# Revit family: Mailboxes_4C-Salsbury_Industries-Rear_Load-9_Door_High_Units
name_source: partatom
category: Specialty Equipment
revit_build: Autodesk Revit 2016 (Build: 20150714_1515(x64)
units: mm (PartAtom-declared; Revit-internal decimal feet)

## family parameters
Always vertical = Yes
Cut with Voids When Loaded = No
Host = Wall
OmniClass Number = 23.40.90.14.11
OmniClass Title = Mail Boxes
Part Type = Normal
Room Calculation Point = No
Round Connector Dimension = Use Diameter
Shared = No

## types (13) — shared parameters
Assembly Code = C1030910
Assembly Description = Mailboxes
Back Enclosure Material = Aluminum - Salsbury Finish - Anodized
Bottom Back Plate = No
Depth = 17.025"
Height = 34.000"
Latch Distance = 9.515"
Latch Locks-Right Side = Yes
Lock Material = Stainless Steel - Salsbury Finish -  Polished
Manufacturer = Salsbury Industries
MasterFormat Number = 10 55 00
MasterFormat Title = Postal Specialties
OmniClass 23 Number = 23.40.90.14.11
OmniClass 23 Title = Mail Boxes
Top Back Plate = No
URL = www.mailboxes.com
Version = 3.0 (06/30/17)

## per-type parameters (varying)
- 3709S-1B RL: Description=9 Door High Unit; Door Slot L1=3700 Series 4C Door Configurations : Empty; Door Slot L2=3700 Series 4C Door Configurations : Empty; Door Slot L3=3700 Series 4C Door Configurations : Empty; Door Slot L4=3700 Series 4C Door Configurations : Empty; Door Slot L5=3700 Series 4C Door Configurations : Empty; Door Slot L6=3700 Series 4C Door Configurations : Empty; Door Slot L7=3700 Series 4C Door Configurations : Empty; Door Slot L8=3700 Series 4C Door Configurations : Empty; Door Slot L9=3700 Series 4C Door Configurations : Empty; Door Slot R1=3700 Series 4C Door Configurations : Empty; Door Slot R2=3700 Series 4C Door Configurations : Empty; Door Slot R3=3700 Series 4C Door Configurations : Empty; Door Slot R4=3700 Series 4C Door Configurations : Empty; Door Slot R5=3700 Series 4C Door Configurations : Empty; Door Slot R6=3700 Series 4C Door Configurations : Empty; Door Slot R7=3700 Series 4C Door Configurations : Empty; Door Slot R8=3700 Series 4C Door Configurations : Empty; Door Slot R9=4C-9 Door High Receptacle; Latch Alignment=13.876"; Latch Locks-Left Side=No; Left Inside Wall=No; Right Inside Wall=No; Type Comments=4C Horizontal Receptacle Bin - Rear Loading; Vertical Center Divider=No; Width=16.344"
- 3709S-1C RL: Description=9 Door High Unit; Door Slot L1=3700 Series 4C Door Configurations : Empty; Door Slot L2=3700 Series 4C Door Configurations : Empty; Door Slot L3=3700 Series 4C Door Configurations : Empty; Door Slot L4=3700 Series 4C Door Configurations : Empty; Door Slot L5=3700 Series 4C Door Configurations : Empty; Door Slot L6=3700 Series 4C Door Configurations : Empty; Door Slot L7=3700 Series 4C Door Configurations : Empty; Door Slot L8=3700 Series 4C Door Configurations : Empty; Door Slot L9=3700 Series 4C Door Configurations : Empty; Door Slot R1=3700 Series 4C Door Configurations : Empty; Door Slot R2=3700 Series 4C Door Configurations : Empty; Door Slot R3=3700 Series 4C Door Configurations : Empty; Door Slot R4=3700 Series 4C Door Configurations : Empty; Door Slot R5=3700 Series 4C Door Configurations : Empty; Door Slot R6=3700 Series 4C Door Configurations : Empty; Door Slot R7=3700 Series 4C Door Configurations : Empty; Door Slot R8=3700 Series 4C Door Configurations : Empty; Door Slot R9=4C-9 Door High Collection Box; Latch Alignment=13.876"; Latch Locks-Left Side=No; Left Inside Wall=No; Right Inside Wall=No; Type Comments=4C Horizontal Collection Box - Rear Loading; Vertical Center Divider=No; Width=16.344"
- 3709D-16 RL: Description=9 Door High Unit:  16 MB1, OM2; Door Slot L1=3700 Series 4C Door Configurations : MB1 Door; Door Slot L2=3700 Series 4C Door Configurations : MB1 Door w/ Divider; Door Slot L3=3700 Series 4C Door Configurations : MB1 Door w/ Divider; Door Slot L4=3700 Series 4C Door Configurations : MB1 Door w/ Divider; Door Slot L5=3700 Series 4C Door Configurations : MB1 Door w/ Divider; Door Slot L6=3700 Series 4C Door Configurations : MB1 Door w/ Divider; Door Slot L7=3700 Series 4C Door Configurations : MB1 Door w/ Divider; Door Slot L8=3700 Series 4C Door Configurations : MB1 Door w/ Divider; Door Slot L9=3700 Series 4C Door Configurations : MB1 Door w/ Divider; Door Slot R1=3700 Series 4C Door Configurations : MB1 Door; Door Slot R2=3700 Series 4C Door Configurations : MB1 Door w/ Divider; Door Slot R3=3700 Series 4C Door Configurations : MB1 Door w/ Divider; Door Slot R4=3700 Series 4C Door Configurations : Empty; Door Slot R5=3700 Series 4C OM2 Configuration : OM2-RL; Door Slot R6=3700 Series 4C Door Configurations : MB1 Door w/ Divider; Door Slot R7=3700 Series 4C Door Configurations : MB1 Door w/ Divider; Door Slot R8=3700 Series 4C Door Configurations : MB1 Door w/ Divider; Door Slot R9=3700 Series 4C Door Configurations : MB1 Door w/ Divider; Latch Alignment=14.857"; Latch Locks-Left Side=Yes; Left Inside Wall=Yes; Right Inside Wall=Yes; Type Comments=4C Standard Horizontal Mailbox - Rear Loading; Vertical Center Divider=Yes; Width=31.098"
- 3709S-07 RL: Description=9 Door High Unit:  7 MB1, OM2; Door Slot L1=3700 Series 4C Door Configurations : Empty; Door Slot L2=3700 Series 4C Door Configurations : Empty; Door Slot L3=3700 Series 4C Door Configurations : Empty; Door Slot L4=3700 Series 4C Door Configurations : Empty; Door Slot L5=3700 Series 4C Door Configurations : Empty; Door Slot L6=3700 Series 4C Door Configurations : Empty; Door Slot L7=3700 Series 4C Door Configurations : Empty; Door Slot L8=3700 Series 4C Door Configurations : Empty; Door Slot L9=3700 Series 4C Door Configurations : Empty; Door Slot R1=3700 Series 4C Door Configurations : MB1 Door; Door Slot R2=3700 Series 4C Door Configurations : MB1 Door w/ Divider; Door Slot R3=3700 Series 4C Door Configurations : MB1 Door w/ Divider; Door Slot R4=3700 Series 4C Door Configurations : Empty; Door Slot R5=3700 Series 4C OM2 Configuration : OM2-RL; Door Slot R6=3700 Series 4C Door Configurations : MB1 Door w/ Divider; Door Slot R7=3700 Series 4C Door Configurations : MB1 Door w/ Divider; Door Slot R8=3700 Series 4C Door Configurations : MB1 Door w/ Divider; Door Slot R9=3700 Series 4C Door Configurations : MB1 Door w/ Divider; Latch Alignment=13.876"; Latch Locks-Left Side=No; Left Inside Wall=No; Right Inside Wall=No; Type Comments=4C Standard Horizontal Mailbox - Rear Loading; Vertical Center Divider=No; Width=16.344"
- 3709D-15 RL: Description=9 Door High Unit:  15 MB1, OM3; Door Slot L1=3700 Series 4C Door Configurations : MB1 Door; Door Slot L2=3700 Series 4C Door Configurations : MB1 Door w/ Divider; Door Slot L3=3700 Series 4C Door Configurations : MB1 Door w/ Divider; Door Slot L4=3700 Series 4C Door Configurations : MB1 Door w/ Divider; Door Slot L5=3700 Series 4C Door Configurations : MB1 Door w/ Divider; Door Slot L6=3700 Series 4C Door Configurations : MB1 Door w/ Divider; Door Slot L7=3700 Series 4C Door Configurations : MB1 Door w/ Divider; Door Slot L8=3700 Series 4C Door Configurations : MB1 Door w/ Divider; Door Slot L9=3700 Series 4C Door Configurations : MB1 Door w/ Divider; Door Slot R1=3700 Series 4C Door Configurations : MB1 Door; Door Slot R2=3700 Series 4C Door Configurations : MB1 Door w/ Divider; Door Slot R3=3700 Series 4C Door Configurations : MB1 Door w/ Divider; Door Slot R4=3700 Series 4C Door Configurations : Empty; Door Slot R5=3700 Series 4C Door Configurations : Empty; Door Slot R6=3700 Series 4C OM3 Configuration : OM3-RL; Door Slot R7=3700 Series 4C Door Configurations : MB1 Door w/ Divider; Door Slot R8=3700 Series 4C Door Configurations : MB1 Door w/ Divider; Door Slot R9=3700 Series 4C Door Configurations : MB1 Door w/ Divider; Latch Alignment=14.857"; Latch Locks-Left Side=Yes; Left Inside Wall=Yes; Right Inside Wall=Yes; Type Comments=4C Standard Horizontal Mailbox - Rear Loading; Vertical Center Divider=Yes; Width=31.098"
- 3709D-10 RL: Description=9 Door High Unit:  10 MB1, 1 PL6, OM2; Door Slot L1=3700 Series 4C Door Configurations : MB1 Door; Door Slot L2=3700 Series 4C Door Configurations : MB1 Door w/ Divider; Door Slot L3=3700 Series 4C Door Configurations : MB1 Door w/ Divider; Door Slot L4=3700 Series 4C Door Configurations : Empty; Door Slot L5=3700 Series 4C Door Configurations : Empty; Door Slot L6=3700 Series 4C Door Configurations : Empty; Door Slot L7=3700 Series 4C Door Configurations : Empty; Door Slot L8=3700 Series 4C Door Configurations : Empty; Door Slot L9=3700 Series 4C Parcel Configurations : PL6 w/ Divider; Door Slot R1=3700 Series 4C Door Configurations : MB1 Door; Door Slot R2=3700 Series 4C Door Configurations : MB1 Door w/ Divider; Door Slot R3=3700 Series 4C Door Configurations : MB1 Door w/ Divider; Door Slot R4=3700 Series 4C Door Configurations : Empty; Door Slot R5=3700 Series 4C OM2 Configuration : OM2-RL; Door Slot R6=3700 Series 4C Door Configurations : MB1 Door w/ Divider; Door Slot R7=3700 Series 4C Door Configurations : MB1 Door w/ Divider; Door Slot R8=3700 Series 4C Door Configurations : MB1 Door w/ Divider; Door Slot R9=3700 Series 4C Door Configurations : MB1 Door w/ Divider; Latch Alignment=14.857"; Latch Locks-Left Side=Yes; Left Inside Wall=Yes; Right Inside Wall=Yes; Type Comments=4C Standard Horizontal Mailbox - Rear Loading; Vertical Center Divider=Yes; Width=31.098"
- 3709D-06 RL: Description=9 Door High Unit:  1 MB1, 5 MB3, OM2; Door Slot L1=3700 Series 4C Door Configurations : Empty; Door Slot L2=3700 Series 4C Door Configurations : Empty; Door Slot L3=3700 Series 4C Door Configurations : MB3 Door; Door Slot L4=3700 Series 4C Door Configurations : Empty; Door Slot L5=3700 Series 4C Door Configurations : Empty; Door Slot L6=3700 Series 4C Door Configurations : MB3 Door w/ Divider; Door Slot L7=3700 Series 4C Door Configurations : Empty; Door Slot L8=3700 Series 4C Door Configurations : Empty; Door Slot L9=3700 Series 4C Door Configurations : MB3 Door w/ Divider; Door Slot R1=3700 Series 4C Door Configurations : Empty; Door Slot R2=3700 Series 4C Door Configurations : Empty; Door Slot R3=3700 Series 4C Door Configurations : MB3 Door; Door Slot R4=3700 Series 4C Door Configurations : Empty; Door Slot R5=3700 Series 4C OM2 Configuration : OM2-RL; Door Slot R6=3700 Series 4C Door Configurations : MB1 Door w/ Divider; Door Slot R7=3700 Series 4C Door Configurations : Empty; Door Slot R8=3700 Series 4C Door Configurations : Empty; Door Slot R9=3700 Series 4C Door Configurations : MB3 Door w/ Divider; Latch Alignment=14.857"; Latch Locks-Left Side=Yes; Left Inside Wall=Yes; Right Inside Wall=Yes; Type Comments=4C Standard Horizontal Mailbox - Rear Loading; Vertical Center Divider=Yes; Width=31.098"
- 3709D-05 RL: Description=9 Door High Unit:  5 MB3, OM3; Door Slot L1=3700 Series 4C Door Configurations : Empty; Door Slot L2=3700 Series 4C Door Configurations : Empty; Door Slot L3=3700 Series 4C Door Configurations : MB3 Door; Door Slot L4=3700 Series 4C Door Configurations : Empty; Door Slot L5=3700 Series 4C Door Configurations : Empty; Door Slot L6=3700 Series 4C Door Configurations : MB3 Door w/ Divider; Door Slot L7=3700 Series 4C Door Configurations : Empty; Door Slot L8=3700 Series 4C Door Configurations : Empty; Door Slot L9=3700 Series 4C Door Configurations : MB3 Door w/ Divider; Door Slot R1=3700 Series 4C Door Configurations : Empty; Door Slot R2=3700 Series 4C Door Configurations : Empty; Door Slot R3=3700 Series 4C Door Configurations : MB3 Door; Door Slot R4=3700 Series 4C Door Configurations : Empty; Door Slot R5=3700 Series 4C Door Configurations : Empty; Door Slot R6=3700 Series 4C OM3 Configuration : OM3-RL; Door Slot R7=3700 Series 4C Door Configurations : Empty; Door Slot R8=3700 Series 4C Door Configurations : Empty; Door Slot R9=3700 Series 4C Door Configurations : MB3 Door w/ Divider; Latch Alignment=14.857"; Latch Locks-Left Side=Yes; Left Inside Wall=Yes; Right Inside Wall=Yes; Type Comments=4C Standard Horizontal Mailbox - Rear Loading; Vertical Center Divider=Yes; Width=31.098"
- 3709D-03 RL: Description=9 Door High Unit:  3 MB3, 1 PL6, OM3; Door Slot L1=3700 Series 4C Door Configurations : Empty; Door Slot L2=3700 Series 4C Door Configurations : Empty; Door Slot L3=3700 Series 4C Door Configurations : MB3 Door; Door Slot L4=3700 Series 4C Door Configurations : Empty; Door Slot L5=3700 Series 4C Door Configurations : Empty; Door Slot L6=3700 Series 4C Door Configurations : Empty; Door Slot L7=3700 Series 4C Door Configurations : Empty; Door Slot L8=3700 Series 4C Door Configurations : Empty; Door Slot L9=3700 Series 4C Parcel Configurations : PL6 w/ Divider; Door Slot R1=3700 Series 4C Door Configurations : Empty; Door Slot R2=3700 Series 4C Door Configurations : Empty; Door Slot R3=3700 Series 4C Door Configurations : MB3 Door; Door Slot R4=3700 Series 4C Door Configurations : Empty; Door Slot R5=3700 Series 4C Door Configurations : Empty; Door Slot R6=3700 Series 4C OM3 Configuration : OM3-RL; Door Slot R7=3700 Series 4C Door Configurations : Empty; Door Slot R8=3700 Series 4C Door Configurations : Empty; Door Slot R9=3700 Series 4C Door Configurations : MB3 Door w/ Divider; Latch Alignment=14.857"; Latch Locks-Left Side=Yes; Left Inside Wall=Yes; Right Inside Wall=Yes; Type Comments=4C Standard Horizontal Mailbox - Rear Loading; Vertical Center Divider=Yes; Width=31.098"
- 3709D-4P RL: Description=9 Door High Unit:  2 PL4, 2 PL5; Door Slot L1=3700 Series 4C Door Configurations : Empty; Door Slot L2=3700 Series 4C Door Configurations : Empty; Door Slot L3=3700 Series 4C Door Configurations : Empty; Door Slot L4=3700 Series 4C Parcel Configurations : PL4; Door Slot L5=3700 Series 4C Door Configurations : Empty; Door Slot L6=3700 Series 4C Door Configurations : Empty; Door Slot L7=3700 Series 4C Door Configurations : Empty; Door Slot L8=3700 Series 4C Door Configurations : Empty; Door Slot L9=3700 Series 4C Parcel Configurations : PL5 w/ Divider; Door Slot R1=3700 Series 4C Door Configurations : Empty; Door Slot R2=3700 Series 4C Door Configurations : Empty; Door Slot R3=3700 Series 4C Door Configurations : Empty; Door Slot R4=3700 Series 4C Parcel Configurations : PL4; Door Slot R5=3700 Series 4C Door Configurations : Empty; Door Slot R6=3700 Series 4C Door Configurations : Empty; Door Slot R7=3700 Series 4C Door Configurations : Empty; Door Slot R8=3700 Series 4C Door Configurations : Empty; Door Slot R9=3700 Series 4C Parcel Configurations : PL5 w/ Divider; Latch Alignment=14.857"; Latch Locks-Left Side=Yes; Left Inside Wall=Yes; Right Inside Wall=Yes; Type Comments=4C Standard Horizontal Mailbox - Rear Loading; Vertical Center Divider=Yes; Width=31.098"
- 3709S-02 RL: Description=9 Door High Unit:  2 MB1, 1 PL5, OM2; Door Slot L1=3700 Series 4C Door Configurations : Empty; Door Slot L2=3700 Series 4C Door Configurations : Empty; Door Slot L3=3700 Series 4C Door Configurations : Empty; Door Slot L4=3700 Series 4C Door Configurations : Empty; Door Slot L5=3700 Series 4C Door Configurations : Empty; Door Slot L6=3700 Series 4C Door Configurations : Empty; Door Slot L7=3700 Series 4C Door Configurations : Empty; Door Slot L8=3700 Series 4C Door Configurations : Empty; Door Slot L9=3700 Series 4C Door Configurations : Empty; Door Slot R1=3700 Series 4C Door Configurations : MB1 Door; Door Slot R2=3700 Series 4C Door Configurations : MB1 Door w/ Divider; Door Slot R3=3700 Series 4C Door Configurations : Empty; Door Slot R4=3700 Series 4C OM2 Configuration : OM2-RL; Door Slot R5=3700 Series 4C Door Configurations : Empty; Door Slot R6=3700 Series 4C Door Configurations : Empty; Door Slot R7=3700 Series 4C Door Configurations : Empty; Door Slot R8=3700 Series 4C Door Configurations : Empty; Door Slot R9=3700 Series 4C Parcel Configurations : PL5 w/ Divider; Latch Alignment=13.876"; Latch Locks-Left Side=No; Left Inside Wall=No; Right Inside Wall=No; Type Comments=4C Standard Horizontal Mailbox - Rear Loading; Vertical Center Divider=No; Width=16.344"
- 3709S-2P RL: Description=9 Door High Unit:  1 PL4, 1 PL5; Door Slot L1=3700 Series 4C Door Configurations : Empty; Door Slot L2=3700 Series 4C Door Configurations : Empty; Door Slot L3=3700 Series 4C Door Configurations : Empty; Door Slot L4=3700 Series 4C Door Configurations : Empty; Door Slot L5=3700 Series 4C Door Configurations : Empty; Door Slot L6=3700 Series 4C Door Configurations : Empty; Door Slot L7=3700 Series 4C Door Configurations : Empty; Door Slot L8=3700 Series 4C Door Configurations : Empty; Door Slot L9=3700 Series 4C Door Configurations : Empty; Door Slot R1=3700 Series 4C Door Configurations : Empty; Door Slot R2=3700 Series 4C Door Configurations : Empty; Door Slot R3=3700 Series 4C Door Configurations : Empty; Door Slot R4=3700 Series 4C Parcel Configurations : PL4; Door Slot R5=3700 Series 4C Door Configurations : Empty; Door Slot R6=3700 Series 4C Door Configurations : Empty; Door Slot R7=3700 Series 4C Door Configurations : Empty; Door Slot R8=3700 Series 4C Door Configurations : Empty; Door Slot R9=3700 Series 4C Parcel Configurations : PL5 w/ Divider; Latch Alignment=13.876"; Latch Locks-Left Side=No; Left Inside Wall=No; Right Inside Wall=No; Type Comments=4C Standard Horizontal Mailbox - Rear Loading; Vertical Center Divider=No; Width=16.344"
- 3709D-04 RL: Description=9 Door High Unit:  1 MB1, 3 MB3, 1 PL6, OM2; Door Slot L1=3700 Series 4C Door Configurations : Empty; Door Slot L2=3700 Series 4C Door Configurations : Empty; Door Slot L3=3700 Series 4C Door Configurations : MB3 Door; Door Slot L4=3700 Series 4C Door Configurations : Empty; Door Slot L5=3700 Series 4C Door Configurations : Empty; Door Slot L6=3700 Series 4C Door Configurations : Empty; Door Slot L7=3700 Series 4C Door Configurations : Empty; Door Slot L8=3700 Series 4C Door Configurations : Empty; Door Slot L9=3700 Series 4C Parcel Configurations : PL6 w/ Divider; Door Slot R1=3700 Series 4C Door Configurations : Empty; Door Slot R2=3700 Series 4C Door Configurations : Empty; Door Slot R3=3700 Series 4C Door Configurations : MB3 Door; Door Slot R4=3700 Series 4C Door Configurations : Empty; Door Slot R5=3700 Series 4C OM2 Configuration : OM2-RL; Door Slot R6=3700 Series 4C Door Configurations : MB1 Door w/ Divider; Door Slot R7=3700 Series 4C Door Configurations : Empty; Door Slot R8=3700 Series 4C Door Configurations : Empty; Door Slot R9=3700 Series 4C Door Configurations : MB3 Door w/ Divider; Latch Alignment=14.857"; Latch Locks-Left Side=Yes; Left Inside Wall=Yes; Right Inside Wall=Yes; Type Comments=4C Standard Horizontal Mailbox - Rear Loading; Vertical Center Divider=Yes; Width=31.098"

note: column(s) folded — value = type name in every type: Model

## geometry (parser evidence)
native form markers: Blend x2, Sweep x24
no freeform markers — native parametric forms only
